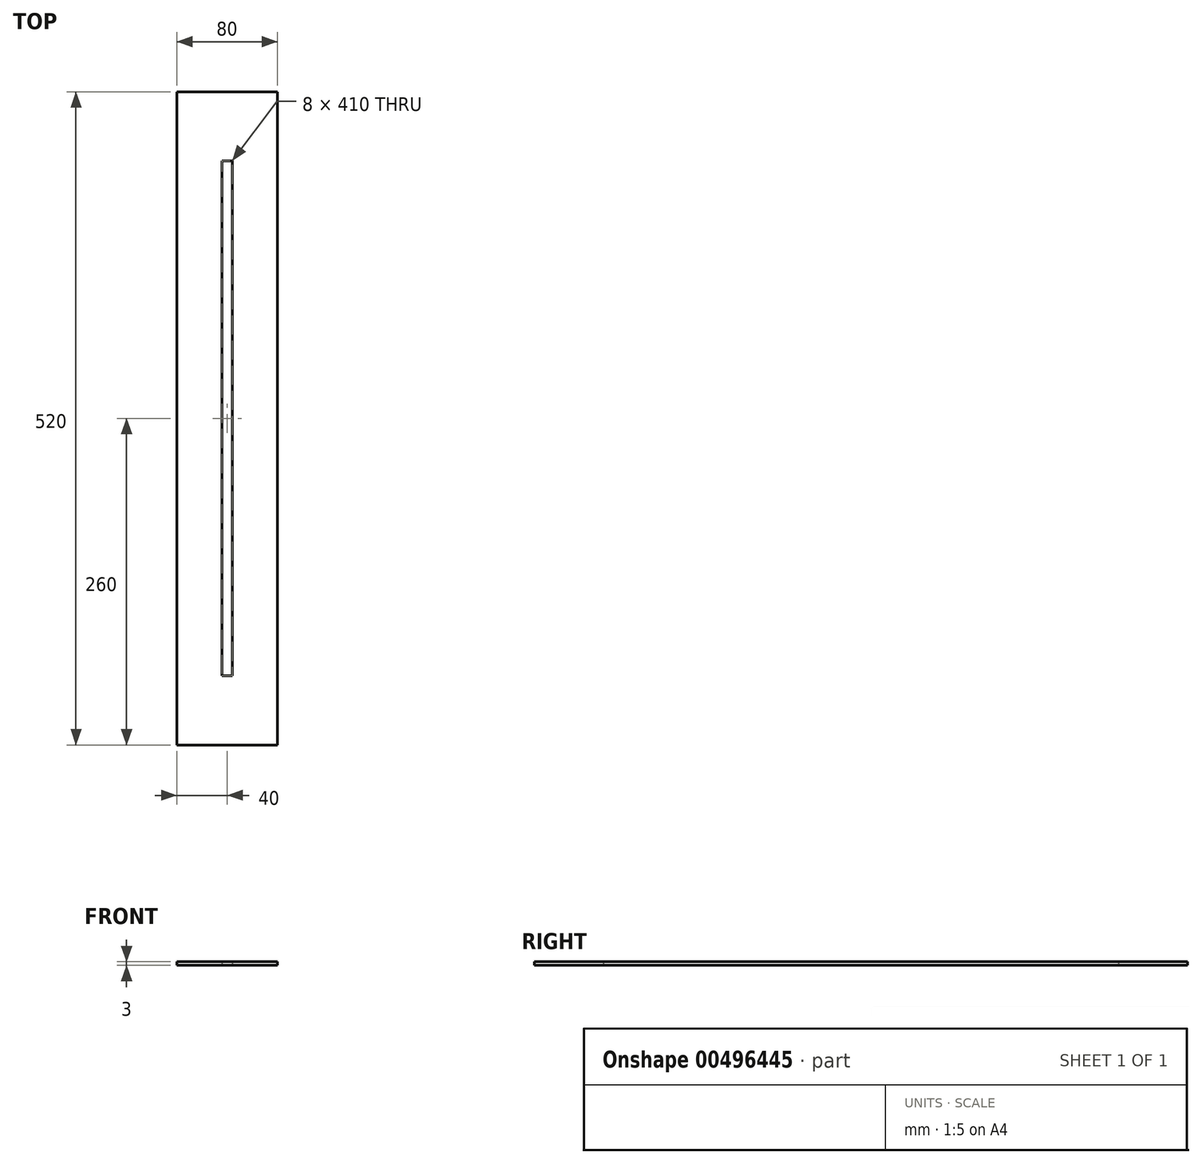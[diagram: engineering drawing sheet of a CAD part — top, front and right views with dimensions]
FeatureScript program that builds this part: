
annotation { "Feature Type Name" : "Feature", "Feature Type Description" : "" }
export const myFeature = defineFeature(function(context is Context, id is Id, definition is map)
    precondition{}
    {
        {
            var Q0;
            Q0=qCreatedBy(makeId("Top.planeOp"),FACE);
            var sketch = newSketch(context, id + "F0", { "sketchPlane" : qUnion([Q0])});
            skLineSegment(sketch, "E0.bottom", {"start": v(0, 0) * mm, "end": v(80, 0) * mm});
            skLineSegment(sketch, "E0.top", {"start": v(0, -520) * mm, "end": v(80, -520) * mm});
            skLineSegment(sketch, "E0.left", {"start": v(0, 0) * mm, "end": v(0, -520) * mm});
            skLineSegment(sketch, "E0.right", {"start": v(80, 0) * mm, "end": v(80, -520) * mm});
            skLineSegment(sketch, "E1.bottom", {"start": v(44, -465) * mm, "end": v(36, -465) * mm});
            skLineSegment(sketch, "E1.top", {"start": v(44, -55) * mm, "end": v(36, -55) * mm});
            skLineSegment(sketch, "E1.left", {"start": v(44, -465) * mm, "end": v(44, -55) * mm});
            skLineSegment(sketch, "E1.right", {"start": v(36, -465) * mm, "end": v(36, -55) * mm});
            skLineSegment(sketch, "E2", {"start": v(40, -465) * mm, "end": v(40, -55) * mm, "construction": true});
            skLineSegment(sketch, "E3", {"start": v(80, -260) * mm, "end": v(-123.99, -260) * mm});
            skPoint(sketch, "E3.endSnap0", {"position": v(80, -260) * mm});
            skSolve(sketch);
        }
        {
            var Q0;
            Q0 = qSketchRegion(id + "F0", true);
            extrude(context, id + "F1", {"entities" : qUnion([Q0]), "depth" : 3 * mm});
        }
    });
